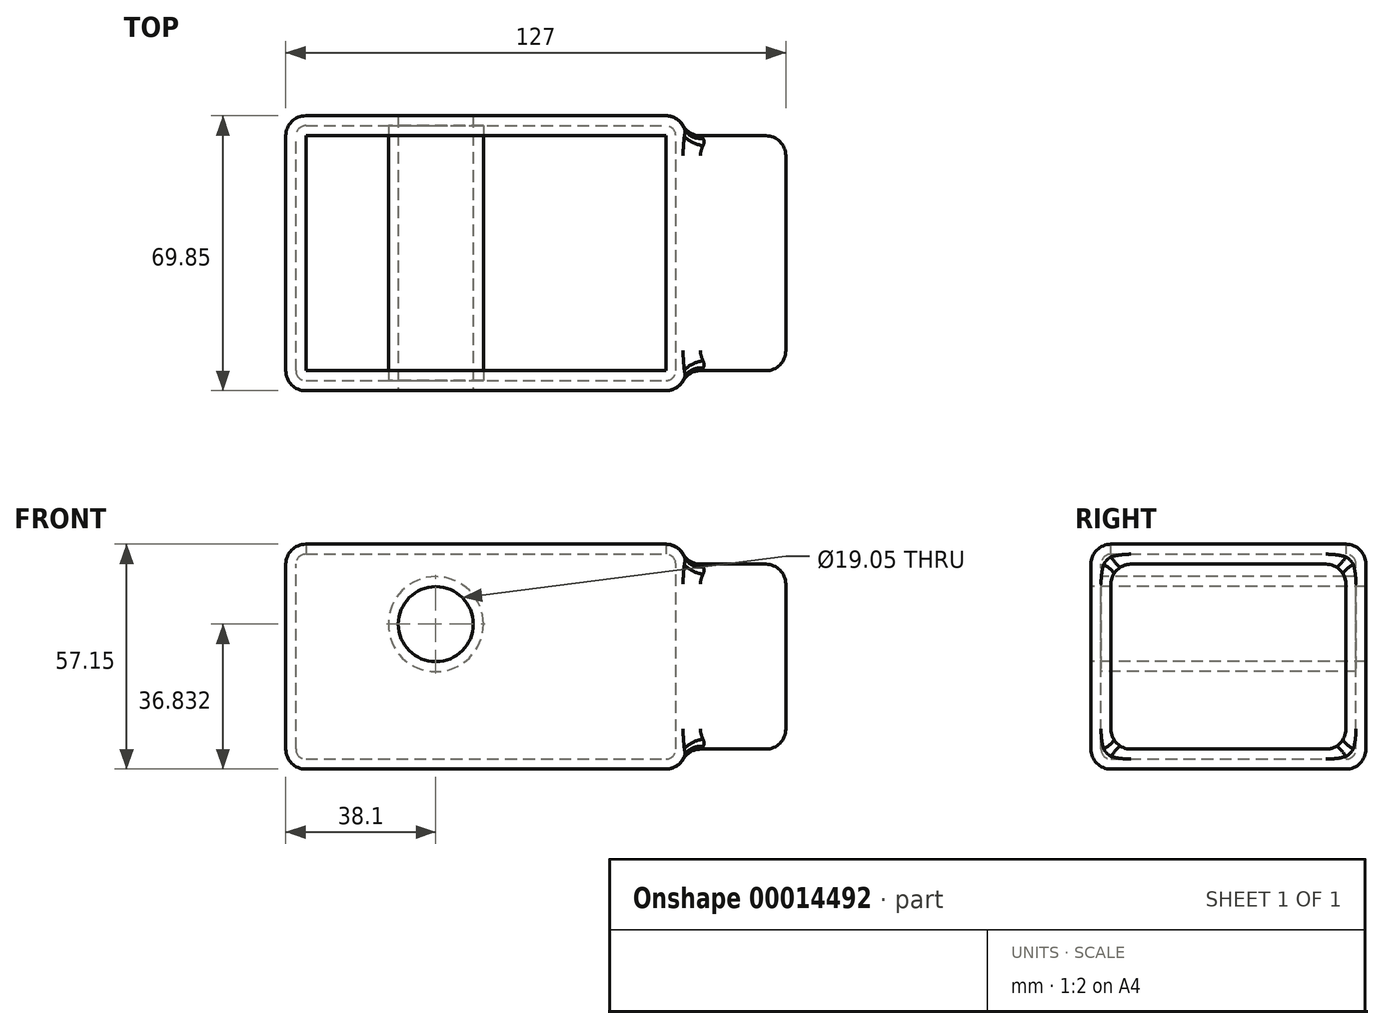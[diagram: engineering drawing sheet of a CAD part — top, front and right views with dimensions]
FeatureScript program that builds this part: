
annotation { "Feature Type Name" : "Feature", "Feature Type Description" : "" }
export const myFeature = defineFeature(function(context is Context, id is Id, definition is map)
    precondition{}
    {
        {
            var Q0;
            Q0=qCreatedBy(makeId("Right.planeOp"),FACE);
            var sketch = newSketch(context, id + "F0", { "sketchPlane" : qUnion([Q0])});
            skLineSegment(sketch, "E0.bottom", {"start": v(-31, 31.6) * mm, "end": v(38.85, 31.6) * mm});
            skLineSegment(sketch, "E0.top", {"start": v(-31, -25.55) * mm, "end": v(38.85, -25.55) * mm});
            skLineSegment(sketch, "E0.left", {"start": v(-31, 31.6) * mm, "end": v(-31, -25.55) * mm});
            skLineSegment(sketch, "E0.right", {"start": v(38.85, 31.6) * mm, "end": v(38.85, -25.55) * mm});
            skSolve(sketch);
        }
        {
            var Q0;
            Q0 = qSketchRegion(id + "F0", true);
            extrude(context, id + "F1", {"entities" : qUnion([Q0]), "depth" : 101.6 * mm});
        }
        {
            var Q0;
            Q0=makeQuery(id+"F1.opExtrude","SWEPT_FACE",FACE,{"disambiguationData":[OSD([sQuery(id+"F0.wireOp",EDGE,"E0.left")])]});
            var sketch = newSketch(context, id + "F2", { "sketchPlane" : qUnion([Q0])});
            skSolve(sketch);
        }
        {
            var Q0;
            {var subQ0=sQuery(id+"F0.wireOp",EDGE,"E0.left");Q0=makeQuery(id+"F2.imprint","IMPRINT",FACE,{"disambiguationData":[TD([[makeQuery(id+"F2.imprint","IMPRINT",EDGE,{"derivedFrom":makeQuery(id+"F1.opExtrude","CAP_EDGE",EDGE,{"disambiguationData":[OSD([subQ0])],"isStart":true})}),1.0]])]});}
            var sketch = newSketch(context, id + "F3", { "sketchPlane" : qUnion([Q0])});
            skCircle(sketch, "E1", {"center": v(38.1, 11.28) * mm, "radius": 9.53 * mm});
            skSolve(sketch);
        }
        {
            var Q0;
            Q0 = qSketchRegion(id + "F3", true);
            extrude(context, id + "F4", {"entities" : qUnion([Q0]), "operationType" : NewBodyOperationType.REMOVE, "endBound" : BoundingType.THROUGH_ALL, "oppositeDirection" : true, "depth" : 25.4 * mm});
        }
        {
            var Q0;
            Q0=makeQuery(id+"F1.opExtrude","CAP_EDGE",EDGE,{"disambiguationData":[OSD([sQuery(id+"F0.wireOp",EDGE,"E0.bottom")])],"isStart":false});
            var Q1;
            Q1=makeQuery(id+"F1.opExtrude","CAP_EDGE",EDGE,{"disambiguationData":[OSD([sQuery(id+"F0.wireOp",EDGE,"E0.right")])],"isStart":false});
            var Q2;
            Q2=makeQuery(id+"F1.opExtrude","CAP_EDGE",EDGE,{"disambiguationData":[OSD([sQuery(id+"F0.wireOp",EDGE,"E0.top")])],"isStart":false});
            var Q3;
            Q3=makeQuery(id+"F1.opExtrude","CAP_EDGE",EDGE,{"disambiguationData":[OSD([sQuery(id+"F0.wireOp",EDGE,"E0.left")])],"isStart":false});
            var Q4;
            Q4=makeQuery(id+"F1.opExtrude","SWEPT_EDGE",EDGE,{"disambiguationData":[OSD([sQuery(id+"F0.wireOp",EDGE,"E0.bottom"),sQuery(id+"F0.wireOp",EDGE,"E0.left")])]});
            var Q5;
            Q5=makeQuery(id+"F1.opExtrude","SWEPT_EDGE",EDGE,{"disambiguationData":[OSD([sQuery(id+"F0.wireOp",EDGE,"E0.bottom"),sQuery(id+"F0.wireOp",EDGE,"E0.right")])]});
            var Q6;
            Q6=makeQuery(id+"F1.opExtrude","CAP_EDGE",EDGE,{"disambiguationData":[OSD([sQuery(id+"F0.wireOp",EDGE,"E0.bottom")])],"isStart":true});
            var Q7;
            Q7=makeQuery(id+"F1.opExtrude","CAP_EDGE",EDGE,{"disambiguationData":[OSD([sQuery(id+"F0.wireOp",EDGE,"E0.left")])],"isStart":true});
            var Q8;
            Q8=makeQuery(id+"F1.opExtrude","SWEPT_EDGE",EDGE,{"disambiguationData":[OSD([sQuery(id+"F0.wireOp",EDGE,"E0.top"),sQuery(id+"F0.wireOp",EDGE,"E0.left")])]});
            var Q9;
            Q9=makeQuery(id+"F1.opExtrude","SWEPT_EDGE",EDGE,{"disambiguationData":[OSD([sQuery(id+"F0.wireOp",EDGE,"E0.top"),sQuery(id+"F0.wireOp",EDGE,"E0.right")])]});
            var Q10;
            Q10=makeQuery(id+"F1.opExtrude","CAP_EDGE",EDGE,{"disambiguationData":[OSD([sQuery(id+"F0.wireOp",EDGE,"E0.top")])],"isStart":true});
            var Q11;
            Q11=makeQuery(id+"F1.opExtrude","CAP_EDGE",EDGE,{"disambiguationData":[OSD([sQuery(id+"F0.wireOp",EDGE,"E0.right")])],"isStart":true});
            fillet(context, id + "F5", {"entities" : qUnion([Q0, Q1, Q2, Q3, Q4, Q5, Q6, Q7, Q8, Q9, Q10, Q11]), "radius" : 5.08 * mm, "tangentPropagation" : true, "allowEdgeOverflow" : false});
        }
        {
            var Q0;
            Q0=makeQuery(id+"F1.opExtrude","SWEPT_FACE",FACE,{"disambiguationData":[OSD([sQuery(id+"F0.wireOp",EDGE,"E0.bottom")])]});
            shell(context, id + "F6", {"entities" : qUnion([Q0]), "thickness" : 2.54 * mm});
        }
        {
            var Q0;
            Q0=makeQuery(id+"F1.opExtrude","CAP_FACE",FACE,{"disambiguationData":[OSD([sQuery(id+"F0.wireOp",EDGE,"E0.bottom"),sQuery(id+"F0.wireOp",EDGE,"E0.top"),sQuery(id+"F0.wireOp",EDGE,"E0.left"),sQuery(id+"F0.wireOp",EDGE,"E0.right")])],"isStart":false});
            extrude(context, id + "F7", {"entities" : qUnion([Q0]), "operationType" : NewBodyOperationType.ADD, "depth" : 25.4 * mm});
        }
        {
            var Q0;
            {var subQ0=sQuery(id+"F0.wireOp",EDGE,"E0.right");var subQ1=sQuery(id+"F0.wireOp",EDGE,"E0.left");var subQ2=sQuery(id+"F0.wireOp",EDGE,"E0.top");var subQ3=sQuery(id+"F0.wireOp",EDGE,"E0.bottom");Q0=makeQuery(id+"F7.opExtrude","CAP_EDGE",EDGE,{"disambiguationData":[OSD([subQ3,subQ2,subQ1,subQ0]),TDD([makeQuery(id+"F5.opFillet","BLEND_EDGE",EDGE,{"blendedFrom":[makeQuery(id+"F1.opExtrude","CAP_EDGE",EDGE,{"disambiguationData":[OSD([subQ3])],"isStart":false}),makeQuery(id+"F1.opExtrude","CAP_FACE",FACE,{"disambiguationData":[OSD([subQ3,subQ2,subQ1,subQ0])],"isStart":false})],"blendedInto":[makeQuery(id+"F1.opExtrude","CAP_FACE",FACE,{"disambiguationData":[OSD([subQ3,subQ2,subQ1,subQ0])],"isStart":false})]})])],"isStart":false});}
            var Q1;
            {var subQ0=sQuery(id+"F0.wireOp",EDGE,"E0.right");var subQ1=sQuery(id+"F0.wireOp",EDGE,"E0.left");var subQ2=sQuery(id+"F0.wireOp",EDGE,"E0.top");var subQ3=sQuery(id+"F0.wireOp",EDGE,"E0.bottom");Q1=makeQuery(id+"F7.opExtrude","CAP_EDGE",EDGE,{"disambiguationData":[OSD([subQ3,subQ2,subQ1,subQ0]),TDD([makeQuery(id+"F5.opFillet","BLEND_EDGE",EDGE,{"blendedFrom":[makeQuery(id+"F1.opExtrude","CAP_EDGE",EDGE,{"disambiguationData":[OSD([subQ0])],"isStart":false}),makeQuery(id+"F1.opExtrude","CAP_FACE",FACE,{"disambiguationData":[OSD([subQ3,subQ2,subQ1,subQ0])],"isStart":false})],"blendedInto":[makeQuery(id+"F1.opExtrude","CAP_FACE",FACE,{"disambiguationData":[OSD([subQ3,subQ2,subQ1,subQ0])],"isStart":false})]})])],"isStart":false});}
            var Q2;
            {var subQ0=sQuery(id+"F0.wireOp",EDGE,"E0.right");var subQ1=sQuery(id+"F0.wireOp",EDGE,"E0.left");var subQ2=sQuery(id+"F0.wireOp",EDGE,"E0.top");var subQ3=sQuery(id+"F0.wireOp",EDGE,"E0.bottom");Q2=makeQuery(id+"F7.opExtrude","CAP_EDGE",EDGE,{"disambiguationData":[OSD([subQ3,subQ2,subQ1,subQ0]),TDD([makeQuery(id+"F5.opFillet","BLEND_EDGE",EDGE,{"blendedFrom":[makeQuery(id+"F1.opExtrude","CAP_EDGE",EDGE,{"disambiguationData":[OSD([subQ1])],"isStart":false}),makeQuery(id+"F1.opExtrude","CAP_FACE",FACE,{"disambiguationData":[OSD([subQ3,subQ2,subQ1,subQ0])],"isStart":false})],"blendedInto":[makeQuery(id+"F1.opExtrude","CAP_FACE",FACE,{"disambiguationData":[OSD([subQ3,subQ2,subQ1,subQ0])],"isStart":false})]})])],"isStart":false});}
            var Q3;
            {var subQ0=sQuery(id+"F0.wireOp",EDGE,"E0.right");var subQ1=sQuery(id+"F0.wireOp",EDGE,"E0.left");var subQ2=sQuery(id+"F0.wireOp",EDGE,"E0.top");var subQ3=sQuery(id+"F0.wireOp",EDGE,"E0.bottom");Q3=makeQuery(id+"F7.opExtrude","CAP_EDGE",EDGE,{"disambiguationData":[OSD([subQ3,subQ2,subQ1,subQ0]),TDD([makeQuery(id+"F5.opFillet","BLEND_EDGE",EDGE,{"blendedFrom":[makeQuery(id+"F1.opExtrude","CAP_EDGE",EDGE,{"disambiguationData":[OSD([subQ2])],"isStart":false}),makeQuery(id+"F1.opExtrude","CAP_FACE",FACE,{"disambiguationData":[OSD([subQ3,subQ2,subQ1,subQ0])],"isStart":false})],"blendedInto":[makeQuery(id+"F1.opExtrude","CAP_FACE",FACE,{"disambiguationData":[OSD([subQ3,subQ2,subQ1,subQ0])],"isStart":false})]})])],"isStart":false});}
            var Q4;
            {var subQ0=sQuery(id+"F0.wireOp",EDGE,"E0.right");var subQ1=sQuery(id+"F0.wireOp",EDGE,"E0.left");var subQ2=sQuery(id+"F0.wireOp",EDGE,"E0.top");var subQ3=sQuery(id+"F0.wireOp",EDGE,"E0.bottom");var subQ4=makeQuery(id+"F5.opFillet","BLEND_EDGE",EDGE,{"blendedFrom":[makeQuery(id+"F1.opExtrude","CAP_EDGE",EDGE,{"disambiguationData":[OSD([subQ3])],"isStart":false}),makeQuery(id+"F1.opExtrude","CAP_FACE",FACE,{"disambiguationData":[OSD([subQ3,subQ2,subQ1,subQ0])],"isStart":false})],"blendedInto":[makeQuery(id+"F1.opExtrude","CAP_FACE",FACE,{"disambiguationData":[OSD([subQ3,subQ2,subQ1,subQ0])],"isStart":false})]});Q4=makeQuery(id+"F7.boolean.opBoolean","MERGE",EDGE,{"derivedFrom":[subQ4,makeQuery(id+"F7.opExtrude","CAP_EDGE",EDGE,{"disambiguationData":[OSD([subQ3,subQ2,subQ1,subQ0]),TDD([subQ4])],"isStart":true})]});}
            var Q5;
            {var subQ0=sQuery(id+"F0.wireOp",EDGE,"E0.right");var subQ1=sQuery(id+"F0.wireOp",EDGE,"E0.left");var subQ2=sQuery(id+"F0.wireOp",EDGE,"E0.top");var subQ3=sQuery(id+"F0.wireOp",EDGE,"E0.bottom");var subQ4=makeQuery(id+"F5.opFillet","BLEND_EDGE",EDGE,{"blendedFrom":[makeQuery(id+"F1.opExtrude","CAP_EDGE",EDGE,{"disambiguationData":[OSD([subQ0])],"isStart":false}),makeQuery(id+"F1.opExtrude","CAP_FACE",FACE,{"disambiguationData":[OSD([subQ3,subQ2,subQ1,subQ0])],"isStart":false})],"blendedInto":[makeQuery(id+"F1.opExtrude","CAP_FACE",FACE,{"disambiguationData":[OSD([subQ3,subQ2,subQ1,subQ0])],"isStart":false})]});Q5=makeQuery(id+"F7.boolean.opBoolean","MERGE",EDGE,{"derivedFrom":[subQ4,makeQuery(id+"F7.opExtrude","CAP_EDGE",EDGE,{"disambiguationData":[OSD([subQ3,subQ2,subQ1,subQ0]),TDD([subQ4])],"isStart":true})]});}
            var Q6;
            {var subQ0=sQuery(id+"F0.wireOp",EDGE,"E0.right");var subQ1=sQuery(id+"F0.wireOp",EDGE,"E0.left");var subQ2=sQuery(id+"F0.wireOp",EDGE,"E0.top");var subQ3=sQuery(id+"F0.wireOp",EDGE,"E0.bottom");var subQ4=makeQuery(id+"F5.opFillet","BLEND_EDGE",EDGE,{"blendedFrom":[makeQuery(id+"F1.opExtrude","CAP_EDGE",EDGE,{"disambiguationData":[OSD([subQ2])],"isStart":false}),makeQuery(id+"F1.opExtrude","CAP_FACE",FACE,{"disambiguationData":[OSD([subQ3,subQ2,subQ1,subQ0])],"isStart":false})],"blendedInto":[makeQuery(id+"F1.opExtrude","CAP_FACE",FACE,{"disambiguationData":[OSD([subQ3,subQ2,subQ1,subQ0])],"isStart":false})]});Q6=makeQuery(id+"F7.boolean.opBoolean","MERGE",EDGE,{"derivedFrom":[subQ4,makeQuery(id+"F7.opExtrude","CAP_EDGE",EDGE,{"disambiguationData":[OSD([subQ3,subQ2,subQ1,subQ0]),TDD([subQ4])],"isStart":true})]});}
            var Q7;
            {var subQ0=sQuery(id+"F0.wireOp",EDGE,"E0.right");var subQ1=sQuery(id+"F0.wireOp",EDGE,"E0.left");var subQ2=sQuery(id+"F0.wireOp",EDGE,"E0.top");var subQ3=sQuery(id+"F0.wireOp",EDGE,"E0.bottom");Q7=makeQuery(id+"F7.opExtrude","SWEPT_EDGE",EDGE,{"disambiguationData":[OSD([subQ3,subQ2,subQ1,subQ0]),TDD([makeQuery(id+"F5.opFillet","BLEND_VERTEX",VERTEX,{"blendedFrom":[makeQuery(id+"F1.opExtrude","CAP_VERTEX",VERTEX,{"disambiguationData":[OSD([subQ2,subQ1])],"isStart":false}),makeQuery(id+"F1.opExtrude","CAP_EDGE",EDGE,{"disambiguationData":[OSD([subQ2])],"isStart":false}),makeQuery(id+"F1.opExtrude","CAP_EDGE",EDGE,{"disambiguationData":[OSD([subQ1])],"isStart":false}),makeQuery(id+"F1.opExtrude","CAP_FACE",FACE,{"disambiguationData":[OSD([subQ3,subQ2,subQ1,subQ0])],"isStart":false})],"blendedInto":[makeQuery(id+"F1.opExtrude","CAP_FACE",FACE,{"disambiguationData":[OSD([subQ3,subQ2,subQ1,subQ0])],"isStart":false})]})])]});}
            var Q8;
            {var subQ0=sQuery(id+"F0.wireOp",EDGE,"E0.right");var subQ1=sQuery(id+"F0.wireOp",EDGE,"E0.left");var subQ2=sQuery(id+"F0.wireOp",EDGE,"E0.top");var subQ3=sQuery(id+"F0.wireOp",EDGE,"E0.bottom");Q8=makeQuery(id+"F7.opExtrude","SWEPT_EDGE",EDGE,{"disambiguationData":[OSD([subQ3,subQ2,subQ1,subQ0]),TDD([makeQuery(id+"F5.opFillet","BLEND_VERTEX",VERTEX,{"blendedFrom":[makeQuery(id+"F1.opExtrude","CAP_VERTEX",VERTEX,{"disambiguationData":[OSD([subQ3,subQ0])],"isStart":false}),makeQuery(id+"F1.opExtrude","CAP_EDGE",EDGE,{"disambiguationData":[OSD([subQ3])],"isStart":false}),makeQuery(id+"F1.opExtrude","CAP_EDGE",EDGE,{"disambiguationData":[OSD([subQ0])],"isStart":false}),makeQuery(id+"F1.opExtrude","CAP_FACE",FACE,{"disambiguationData":[OSD([subQ3,subQ2,subQ1,subQ0])],"isStart":false})],"blendedInto":[makeQuery(id+"F1.opExtrude","CAP_FACE",FACE,{"disambiguationData":[OSD([subQ3,subQ2,subQ1,subQ0])],"isStart":false})]})])]});}
            var Q9;
            {var subQ0=sQuery(id+"F0.wireOp",EDGE,"E0.right");var subQ1=sQuery(id+"F0.wireOp",EDGE,"E0.left");var subQ2=sQuery(id+"F0.wireOp",EDGE,"E0.top");var subQ3=sQuery(id+"F0.wireOp",EDGE,"E0.bottom");Q9=makeQuery(id+"F7.opExtrude","SWEPT_EDGE",EDGE,{"disambiguationData":[OSD([subQ3,subQ2,subQ1,subQ0]),TDD([makeQuery(id+"F5.opFillet","BLEND_VERTEX",VERTEX,{"blendedFrom":[makeQuery(id+"F1.opExtrude","CAP_VERTEX",VERTEX,{"disambiguationData":[OSD([subQ3,subQ1])],"isStart":false}),makeQuery(id+"F1.opExtrude","CAP_EDGE",EDGE,{"disambiguationData":[OSD([subQ3])],"isStart":false}),makeQuery(id+"F1.opExtrude","CAP_EDGE",EDGE,{"disambiguationData":[OSD([subQ1])],"isStart":false}),makeQuery(id+"F1.opExtrude","CAP_FACE",FACE,{"disambiguationData":[OSD([subQ3,subQ2,subQ1,subQ0])],"isStart":false})],"blendedInto":[makeQuery(id+"F1.opExtrude","CAP_FACE",FACE,{"disambiguationData":[OSD([subQ3,subQ2,subQ1,subQ0])],"isStart":false})]})])]});}
            var Q10;
            {var subQ0=sQuery(id+"F0.wireOp",EDGE,"E0.right");var subQ1=sQuery(id+"F0.wireOp",EDGE,"E0.left");var subQ2=sQuery(id+"F0.wireOp",EDGE,"E0.top");var subQ3=sQuery(id+"F0.wireOp",EDGE,"E0.bottom");Q10=makeQuery(id+"F7.opExtrude","SWEPT_EDGE",EDGE,{"disambiguationData":[OSD([subQ3,subQ2,subQ1,subQ0]),TDD([makeQuery(id+"F5.opFillet","BLEND_VERTEX",VERTEX,{"blendedFrom":[makeQuery(id+"F1.opExtrude","CAP_VERTEX",VERTEX,{"disambiguationData":[OSD([subQ2,subQ0])],"isStart":false}),makeQuery(id+"F1.opExtrude","CAP_EDGE",EDGE,{"disambiguationData":[OSD([subQ2])],"isStart":false}),makeQuery(id+"F1.opExtrude","CAP_EDGE",EDGE,{"disambiguationData":[OSD([subQ0])],"isStart":false}),makeQuery(id+"F1.opExtrude","CAP_FACE",FACE,{"disambiguationData":[OSD([subQ3,subQ2,subQ1,subQ0])],"isStart":false})],"blendedInto":[makeQuery(id+"F1.opExtrude","CAP_FACE",FACE,{"disambiguationData":[OSD([subQ3,subQ2,subQ1,subQ0])],"isStart":false})]})])]});}
            var Q11;
            {var subQ0=sQuery(id+"F0.wireOp",EDGE,"E0.right");var subQ1=sQuery(id+"F0.wireOp",EDGE,"E0.left");var subQ2=sQuery(id+"F0.wireOp",EDGE,"E0.top");var subQ3=sQuery(id+"F0.wireOp",EDGE,"E0.bottom");var subQ4=makeQuery(id+"F5.opFillet","BLEND_EDGE",EDGE,{"blendedFrom":[makeQuery(id+"F1.opExtrude","CAP_EDGE",EDGE,{"disambiguationData":[OSD([subQ1])],"isStart":false}),makeQuery(id+"F1.opExtrude","CAP_FACE",FACE,{"disambiguationData":[OSD([subQ3,subQ2,subQ1,subQ0])],"isStart":false})],"blendedInto":[makeQuery(id+"F1.opExtrude","CAP_FACE",FACE,{"disambiguationData":[OSD([subQ3,subQ2,subQ1,subQ0])],"isStart":false})]});Q11=makeQuery(id+"F7.boolean.opBoolean","MERGE",EDGE,{"derivedFrom":[subQ4,makeQuery(id+"F7.opExtrude","CAP_EDGE",EDGE,{"disambiguationData":[OSD([subQ3,subQ2,subQ1,subQ0]),TDD([subQ4])],"isStart":true})]});}
            fillet(context, id + "F8", {"entities" : qUnion([Q0, Q1, Q2, Q3, Q4, Q5, Q6, Q7, Q8, Q9, Q10, Q11]), "radius" : 5.08 * mm, "tangentPropagation" : true, "allowEdgeOverflow" : false});
        }
    });
